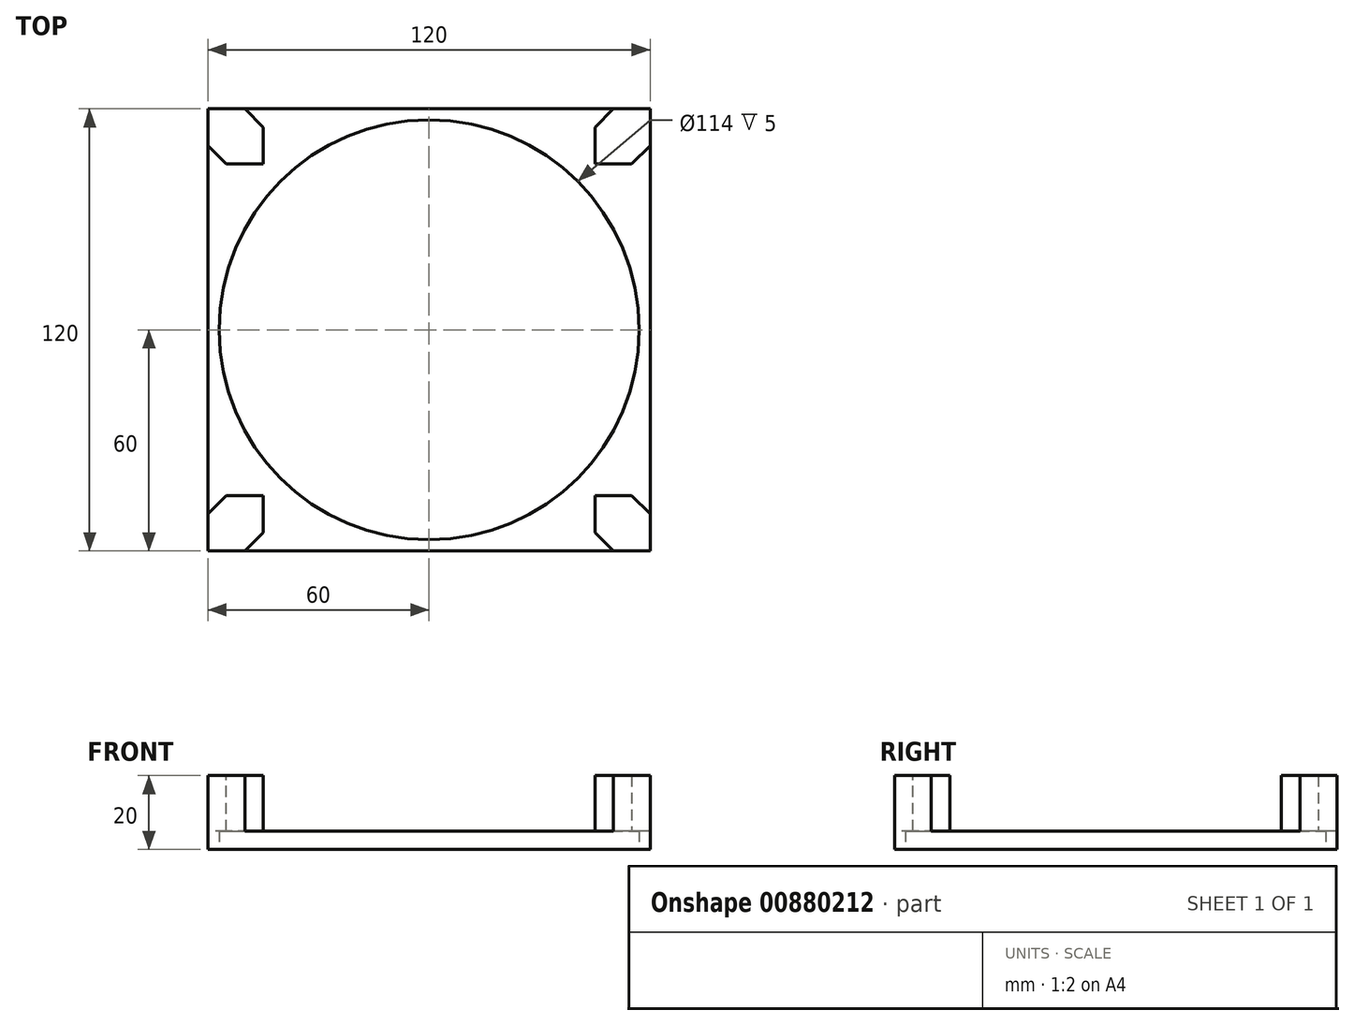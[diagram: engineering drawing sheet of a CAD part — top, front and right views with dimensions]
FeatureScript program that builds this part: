
annotation { "Feature Type Name" : "Feature", "Feature Type Description" : "" }
export const myFeature = defineFeature(function(context is Context, id is Id, definition is map)
    precondition{}
    {
        {
            var Q0;
            Q0=qCreatedBy(makeId("Top.planeOp"),FACE);
            var sketch = newSketch(context, id + "F0", { "sketchPlane" : qUnion([Q0])});
            skLineSegment(sketch, "E0.bottom", {"start": v(60, -60) * mm, "end": v(-60, -60) * mm});
            skLineSegment(sketch, "E0.top", {"start": v(60, 60) * mm, "end": v(-60, 60) * mm});
            skLineSegment(sketch, "E0.left", {"start": v(60, -60) * mm, "end": v(60, 60) * mm});
            skLineSegment(sketch, "E0.right", {"start": v(-60, -60) * mm, "end": v(-60, 60) * mm});
            skPoint(sketch, "E0.middle", {"position": v(0, 0) * mm});
            skCircle(sketch, "E1", {"center": v(0, 0) * mm, "radius": 57 * mm});
            skLineSegment(sketch, "E2.bottom", {"start": v(-60, 60) * mm, "end": v(-45, 60) * mm});
            skLineSegment(sketch, "E2.top", {"start": v(-60, 45) * mm, "end": v(-45, 45) * mm});
            skLineSegment(sketch, "E2.left", {"start": v(-60, 60) * mm, "end": v(-60, 45) * mm});
            skLineSegment(sketch, "E2.right", {"start": v(-45, 60) * mm, "end": v(-45, 45) * mm});
            skLineSegment(sketch, "E3.bottom", {"start": v(60, 60) * mm, "end": v(45, 60) * mm});
            skLineSegment(sketch, "E3.top", {"start": v(60, 45) * mm, "end": v(45, 45) * mm});
            skLineSegment(sketch, "E3.left", {"start": v(60, 60) * mm, "end": v(60, 45) * mm});
            skLineSegment(sketch, "E3.right", {"start": v(45, 60) * mm, "end": v(45, 45) * mm});
            skLineSegment(sketch, "E4.bottom", {"start": v(-60, -60) * mm, "end": v(-45, -60) * mm});
            skLineSegment(sketch, "E4.top", {"start": v(-60, -45) * mm, "end": v(-45, -45) * mm});
            skLineSegment(sketch, "E4.left", {"start": v(-60, -60) * mm, "end": v(-60, -45) * mm});
            skLineSegment(sketch, "E4.right", {"start": v(-45, -60) * mm, "end": v(-45, -45) * mm});
            skPoint(sketch, "E5.oppositeSnap0", {"position": v(-52.5, -45) * mm});
            skLineSegment(sketch, "E5.bottom", {"start": v(60, -60) * mm, "end": v(45, -60) * mm});
            skLineSegment(sketch, "E5.top", {"start": v(60, -45) * mm, "end": v(45, -45) * mm});
            skLineSegment(sketch, "E5.left", {"start": v(60, -60) * mm, "end": v(60, -45) * mm});
            skLineSegment(sketch, "E5.right", {"start": v(45, -60) * mm, "end": v(45, -45) * mm});
            skSolve(sketch);
        }
        {
            var Q0;
            Q0=makeQuery(id+"F0.imprint","IMPRINT",FACE,{"disambiguationData":[TD([[makeQuery(id+"F0.imprint","IMPRINT",EDGE,{"derivedFrom":sQuery(id+"F0.wireOp",EDGE,"E1")}),-1.0]])]});
            extrude(context, id + "F1", {"entities" : qUnion([Q0]), "depth" : 5 * mm, "offsetDistance" : 25 * mm});
        }
        {
            var Q0;
            {var subQ4=sQuery(id+"F0.wireOp",EDGE,"E2.top");Q0=makeQuery(id+"F0.imprint","IMPRINT",FACE,{"disambiguationData":[TD([[makeQuery(id+"F0.imprint","IMPRINT",EDGE,{"derivedFrom":subQ4}),1.0]])]});}
            var Q1;
            {var subQ4=sQuery(id+"F0.wireOp",EDGE,"E3.top");Q1=makeQuery(id+"F0.imprint","IMPRINT",FACE,{"disambiguationData":[TD([[makeQuery(id+"F0.imprint","IMPRINT",EDGE,{"derivedFrom":subQ4}),-1.0]])]});}
            var Q2;
            {var subQ4=sQuery(id+"F0.wireOp",EDGE,"E5.top");Q2=makeQuery(id+"F0.imprint","IMPRINT",FACE,{"disambiguationData":[TD([[makeQuery(id+"F0.imprint","IMPRINT",EDGE,{"derivedFrom":subQ4}),1.0]])]});}
            var Q3;
            {var subQ4=sQuery(id+"F0.wireOp",EDGE,"E4.top");Q3=makeQuery(id+"F0.imprint","IMPRINT",FACE,{"disambiguationData":[TD([[makeQuery(id+"F0.imprint","IMPRINT",EDGE,{"derivedFrom":subQ4}),-1.0]])]});}
            extrude(context, id + "F2", {"entities" : qUnion([Q0, Q1, Q2, Q3]), "operationType" : NewBodyOperationType.ADD, "depth" : 20 * mm, "offsetDistance" : 25 * mm});
        }
        {
            var Q0;
            Q0=makeQuery(id+"F2.opExtrude","SWEPT_EDGE",EDGE,{"disambiguationData":[OSD([sQuery(id+"F0.wireOp",EDGE,"E0.right"),sQuery(id+"F0.wireOp",EDGE,"E4.top")])]});
            var Q1;
            Q1=makeQuery(id+"F2.opExtrude","SWEPT_EDGE",EDGE,{"disambiguationData":[OSD([sQuery(id+"F0.wireOp",EDGE,"E0.bottom"),sQuery(id+"F0.wireOp",EDGE,"E4.right")])]});
            var Q2;
            Q2=makeQuery(id+"F2.opExtrude","SWEPT_EDGE",EDGE,{"disambiguationData":[OSD([sQuery(id+"F0.wireOp",EDGE,"E0.bottom"),sQuery(id+"F0.wireOp",EDGE,"E5.right")])]});
            var Q3;
            Q3=makeQuery(id+"F2.opExtrude","SWEPT_EDGE",EDGE,{"disambiguationData":[OSD([sQuery(id+"F0.wireOp",EDGE,"E0.left"),sQuery(id+"F0.wireOp",EDGE,"E5.top")])]});
            var Q4;
            Q4=makeQuery(id+"F2.opExtrude","SWEPT_EDGE",EDGE,{"disambiguationData":[OSD([sQuery(id+"F0.wireOp",EDGE,"E0.top"),sQuery(id+"F0.wireOp",EDGE,"E3.right")])]});
            var Q5;
            Q5=makeQuery(id+"F2.opExtrude","SWEPT_EDGE",EDGE,{"disambiguationData":[OSD([sQuery(id+"F0.wireOp",EDGE,"E0.left"),sQuery(id+"F0.wireOp",EDGE,"E3.top")])]});
            var Q6;
            Q6=makeQuery(id+"F2.opExtrude","SWEPT_EDGE",EDGE,{"disambiguationData":[OSD([sQuery(id+"F0.wireOp",EDGE,"E0.right"),sQuery(id+"F0.wireOp",EDGE,"E2.top")])]});
            var Q7;
            Q7=makeQuery(id+"F2.opExtrude","SWEPT_EDGE",EDGE,{"disambiguationData":[OSD([sQuery(id+"F0.wireOp",EDGE,"E0.top"),sQuery(id+"F0.wireOp",EDGE,"E2.right")])]});
            chamfer(context, id + "F3", {"entities" : qUnion([Q0, Q1, Q2, Q3, Q4, Q5, Q6, Q7]), "width" : 5 * mm, "tangentPropagation" : true});
        }
    });
